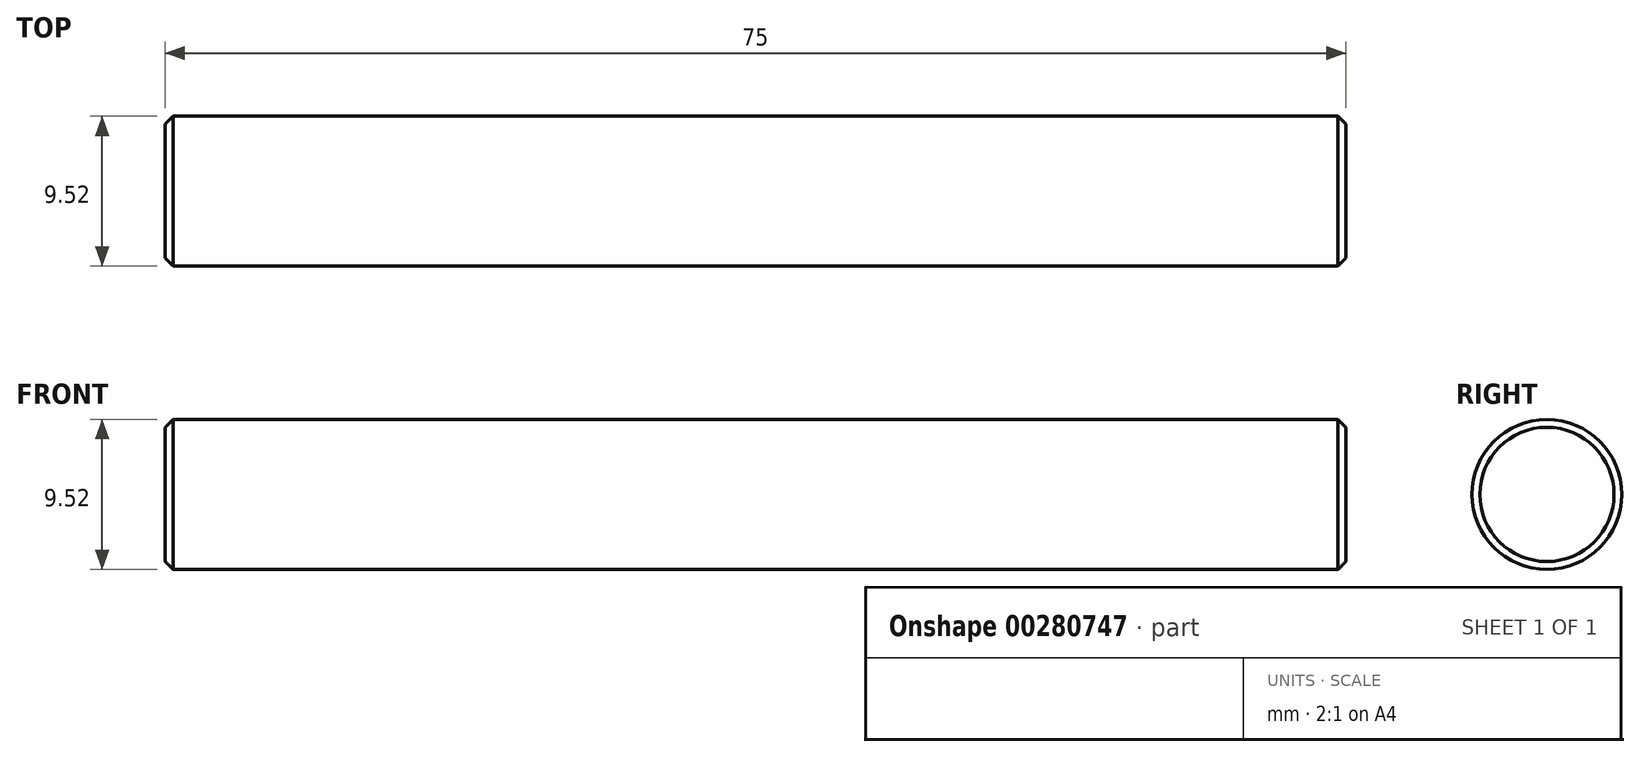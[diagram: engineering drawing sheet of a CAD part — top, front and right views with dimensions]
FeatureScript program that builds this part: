
annotation { "Feature Type Name" : "Feature", "Feature Type Description" : "" }
export const myFeature = defineFeature(function(context is Context, id is Id, definition is map)
    precondition{}
    {
        {
            var Q0;
            Q0=qCreatedBy(makeId("Right.planeOp"),FACE);
            var sketch = newSketch(context, id + "F0", { "sketchPlane" : qUnion([Q0])});
            skCircle(sketch, "E0", {"center": v(0, 0) * mm, "radius": 4.76 * mm});
            skSolve(sketch);
        }
        {
            var Q0;
            Q0 = qSketchRegion(id + "F0", true);
            extrude(context, id + "F1", {"entities" : qUnion([Q0]), "depth" : 75 * mm});
        }
        {
            var Q0;
            Q0=makeQuery(id+"F1.opExtrude","CAP_EDGE",EDGE,{"disambiguationData":[OSD([sQuery(id+"F0.wireOp",EDGE,"E0")])],"isStart":false});
            var Q1;
            Q1=makeQuery(id+"F1.opExtrude","CAP_EDGE",EDGE,{"disambiguationData":[OSD([sQuery(id+"F0.wireOp",EDGE,"E0")])],"isStart":true});
            chamfer(context, id + "F2", {"entities" : qUnion([Q0, Q1]), "width" : .5 * mm, "tangentPropagation" : true});
        }
    });
